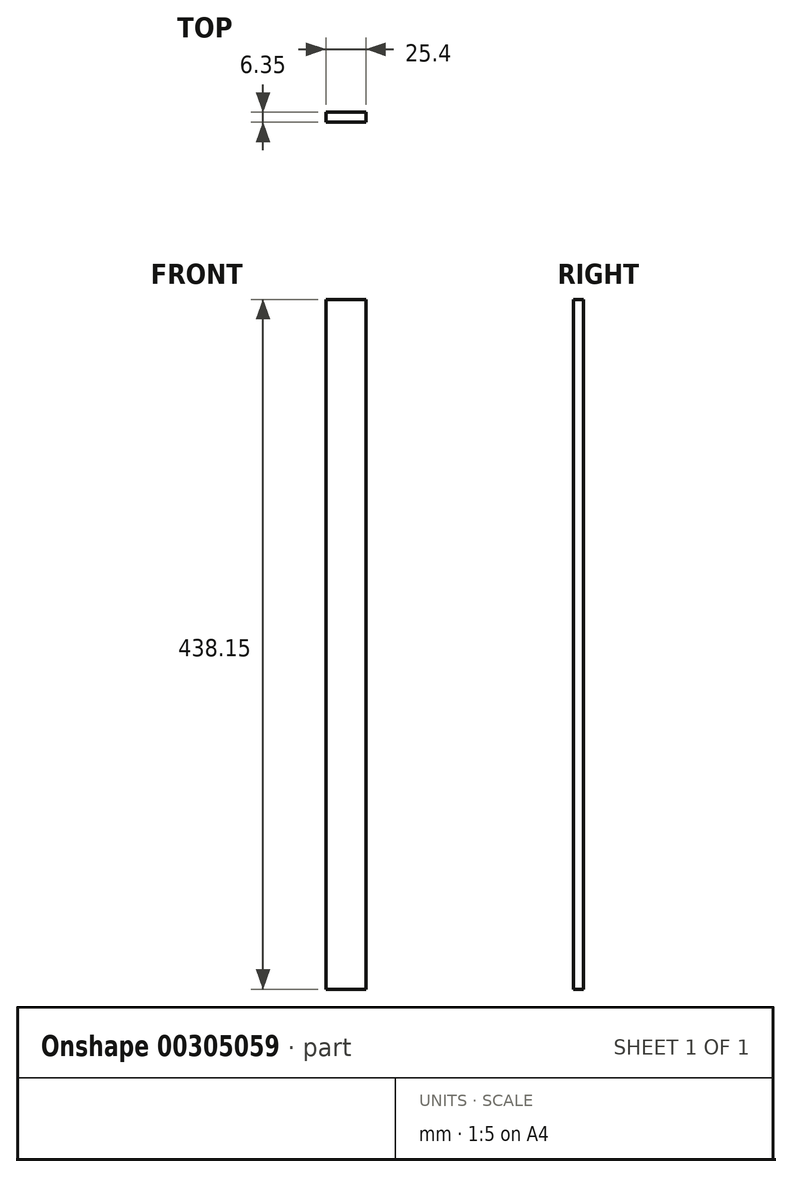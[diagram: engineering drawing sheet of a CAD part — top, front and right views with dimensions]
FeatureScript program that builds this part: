
annotation { "Feature Type Name" : "Feature", "Feature Type Description" : "" }
export const myFeature = defineFeature(function(context is Context, id is Id, definition is map)
    precondition{}
    {
        {
            var Q0;
            Q0=qCreatedBy(makeId("Front.planeOp"),FACE);
            var sketch = newSketch(context, id + "F0", { "sketchPlane" : qUnion([Q0])});
            skLineSegment(sketch, "E0.bottom", {"start": v(-12.7, 12.7) * mm, "end": v(12.7, 12.7) * mm});
            skLineSegment(sketch, "E0.top", {"start": v(-12.7, -425.45) * mm, "end": v(12.7, -425.45) * mm});
            skLineSegment(sketch, "E0.left", {"start": v(-12.7, 12.7) * mm, "end": v(-12.7, -425.45) * mm});
            skLineSegment(sketch, "E0.right", {"start": v(12.7, 12.7) * mm, "end": v(12.7, -425.45) * mm});
            skPoint(sketch, "E1", {"position": v(0, 12.7) * mm});
            skPoint(sketch, "E2", {"position": v(0, 0) * mm});
            skSolve(sketch);
        }
        {
            var Q0;
            Q0=makeQuery(id+"F0.imprint","IMPRINT",FACE,{"disambiguationData":[TD([[makeQuery(id+"F0.imprint","IMPRINT",EDGE,{"derivedFrom":sQuery(id+"F0.wireOp",EDGE,"E0.bottom")}),-1.0]])]});
            extrude(context, id + "F1", {"entities" : qUnion([Q0]), "depth" : 6.35 * mm});
        }
    });
